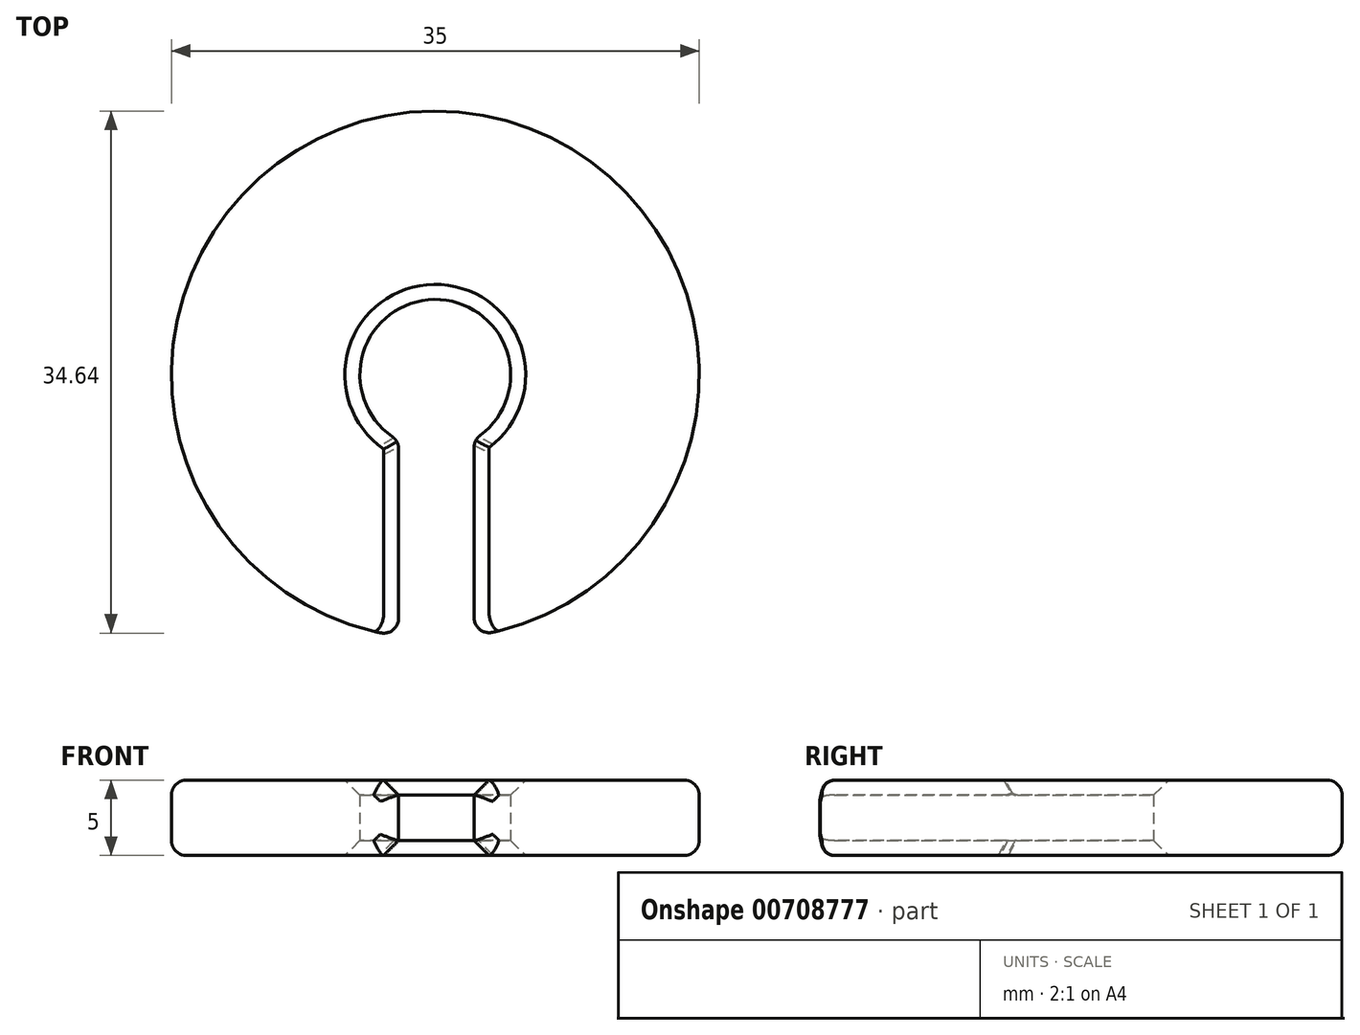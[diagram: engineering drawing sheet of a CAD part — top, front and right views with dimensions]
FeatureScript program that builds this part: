
annotation { "Feature Type Name" : "Feature", "Feature Type Description" : "" }
export const myFeature = defineFeature(function(context is Context, id is Id, definition is map)
    precondition{}
    {
        {
            var Q0;
            Q0=qCreatedBy(makeId("Top.planeOp"),FACE);
            var sketch = newSketch(context, id + "F0", { "sketchPlane" : qUnion([Q0])});
            skCircle(sketch, "E0", {"center": v(-4.66, 0) * mm, "radius": 5 * mm});
            skCircle(sketch, "E1", {"center": v(-4.66, 0) * mm, "radius": 17.5 * mm});
            skLineSegment(sketch, "E2", {"start": v(-7.08, -4.37) * mm, "end": v(-7.08, -24.29) * mm});
            skLineSegment(sketch, "E3", {"start": v(-7.08, -24.29) * mm, "end": v(-2.08, -24.29) * mm});
            skLineSegment(sketch, "E4", {"start": v(-2.08, -24.29) * mm, "end": v(-2.08, -4.29) * mm});
            skSolve(sketch);
        }
        {
            var Q0;
            {var subQ0=sQuery(id+"F0.wireOp",EDGE,"E2");var subQ1=sQuery(id+"F0.wireOp",EDGE,"E0");var subQ2=makeQuery(id+"F0.imprint","INTERSECT",VERTEX,{"derivedFrom":[subQ1,subQ0]});Q0=makeQuery(id+"F0.imprint","IMPRINT",FACE,{"disambiguationData":[TD([[makeQuery(id+"F0.imprint","IMPRINT",EDGE,{"disambiguationData":[TD([[subQ2,1.0]])],"derivedFrom":subQ1}),-1.0]])]});}
            extrude(context, id + "F1", {"entities" : qUnion([Q0]), "depth" : 5 * mm, "offsetDistance" : 25.4 * mm});
        }
        {
            var Q0;
            Q0=makeQuery(id+"F1.opExtrude","CAP_EDGE",EDGE,{"disambiguationData":[OSD([sQuery(id+"F0.wireOp",EDGE,"E2")])],"isStart":false});
            var Q1;
            Q1=makeQuery(id+"F1.opExtrude","CAP_EDGE",EDGE,{"disambiguationData":[OSD([sQuery(id+"F0.wireOp",EDGE,"E0")])],"isStart":false});
            var Q2;
            Q2=makeQuery(id+"F1.opExtrude","CAP_EDGE",EDGE,{"disambiguationData":[OSD([sQuery(id+"F0.wireOp",EDGE,"E4")])],"isStart":false});
            var Q3;
            Q3=makeQuery(id+"F1.opExtrude","CAP_EDGE",EDGE,{"disambiguationData":[OSD([sQuery(id+"F0.wireOp",EDGE,"E2")])],"isStart":true});
            var Q4;
            Q4=makeQuery(id+"F1.opExtrude","CAP_EDGE",EDGE,{"disambiguationData":[OSD([sQuery(id+"F0.wireOp",EDGE,"E4")])],"isStart":true});
            var Q5;
            Q5=makeQuery(id+"F1.opExtrude","CAP_EDGE",EDGE,{"disambiguationData":[OSD([sQuery(id+"F0.wireOp",EDGE,"E0")])],"isStart":true});
            chamfer(context, id + "F2", {"entities" : qUnion([Q0, Q1, Q2, Q3, Q4, Q5]), "width" : 1 * mm, "tangentPropagation" : true});
        }
        {
            var Q0;
            Q0=makeQuery(id+"F1.opExtrude","CAP_EDGE",EDGE,{"disambiguationData":[OSD([sQuery(id+"F0.wireOp",EDGE,"E1")])],"isStart":true});
            var Q1;
            Q1=makeQuery(id+"F1.opExtrude","CAP_EDGE",EDGE,{"disambiguationData":[OSD([sQuery(id+"F0.wireOp",EDGE,"E1")])],"isStart":false});
            var Q2;
            Q2=makeQuery(id+"F1.opExtrude","SWEPT_EDGE",EDGE,{"disambiguationData":[OSD([sQuery(id+"F0.wireOp",EDGE,"E1"),sQuery(id+"F0.wireOp",EDGE,"E4")])]});
            var Q3;
            Q3=makeQuery(id+"F2.opChamfer","BLEND_EDGE",EDGE,{"blendedFrom":[makeQuery(id+"F1.opExtrude","CAP_EDGE",EDGE,{"disambiguationData":[OSD([sQuery(id+"F0.wireOp",EDGE,"E4")])],"isStart":false}),makeQuery(id+"F1.opExtrude","SWEPT_FACE",FACE,{"disambiguationData":[OSD([sQuery(id+"F0.wireOp",EDGE,"E1")])]})],"blendedInto":[makeQuery(id+"F1.opExtrude","SWEPT_FACE",FACE,{"disambiguationData":[OSD([sQuery(id+"F0.wireOp",EDGE,"E1")])]})]});
            var Q4;
            Q4=makeQuery(id+"F2.opChamfer","BLEND_EDGE",EDGE,{"blendedFrom":[makeQuery(id+"F1.opExtrude","CAP_EDGE",EDGE,{"disambiguationData":[OSD([sQuery(id+"F0.wireOp",EDGE,"E4")])],"isStart":true}),makeQuery(id+"F1.opExtrude","SWEPT_FACE",FACE,{"disambiguationData":[OSD([sQuery(id+"F0.wireOp",EDGE,"E1")])]})],"blendedInto":[makeQuery(id+"F1.opExtrude","SWEPT_FACE",FACE,{"disambiguationData":[OSD([sQuery(id+"F0.wireOp",EDGE,"E1")])]})]});
            var Q5;
            Q5=makeQuery(id+"F2.opChamfer","BLEND_EDGE",EDGE,{"blendedFrom":[makeQuery(id+"F1.opExtrude","CAP_EDGE",EDGE,{"disambiguationData":[OSD([sQuery(id+"F0.wireOp",EDGE,"E2")])],"isStart":true}),makeQuery(id+"F1.opExtrude","SWEPT_FACE",FACE,{"disambiguationData":[OSD([sQuery(id+"F0.wireOp",EDGE,"E1")])]})],"blendedInto":[makeQuery(id+"F1.opExtrude","SWEPT_FACE",FACE,{"disambiguationData":[OSD([sQuery(id+"F0.wireOp",EDGE,"E1")])]})]});
            var Q6;
            Q6=makeQuery(id+"F1.opExtrude","SWEPT_EDGE",EDGE,{"disambiguationData":[OSD([sQuery(id+"F0.wireOp",EDGE,"E1"),sQuery(id+"F0.wireOp",EDGE,"E2")])]});
            var Q7;
            Q7=makeQuery(id+"F2.opChamfer","BLEND_EDGE",EDGE,{"blendedFrom":[makeQuery(id+"F1.opExtrude","CAP_EDGE",EDGE,{"disambiguationData":[OSD([sQuery(id+"F0.wireOp",EDGE,"E2")])],"isStart":false}),makeQuery(id+"F1.opExtrude","SWEPT_FACE",FACE,{"disambiguationData":[OSD([sQuery(id+"F0.wireOp",EDGE,"E1")])]})],"blendedInto":[makeQuery(id+"F1.opExtrude","SWEPT_FACE",FACE,{"disambiguationData":[OSD([sQuery(id+"F0.wireOp",EDGE,"E1")])]})]});
            var Q8;
            Q8=makeQuery(id+"F1.opExtrude","SWEPT_EDGE",EDGE,{"disambiguationData":[OSD([sQuery(id+"F0.wireOp",EDGE,"E0"),sQuery(id+"F0.wireOp",EDGE,"E4")])]});
            var Q9;
            Q9=makeQuery(id+"F2.opChamfer","BLEND_EDGE",EDGE,{"blendedFrom":[makeQuery(id+"F1.opExtrude","CAP_EDGE",EDGE,{"disambiguationData":[OSD([sQuery(id+"F0.wireOp",EDGE,"E0")])],"isStart":true}),makeQuery(id+"F1.opExtrude","CAP_EDGE",EDGE,{"disambiguationData":[OSD([sQuery(id+"F0.wireOp",EDGE,"E4")])],"isStart":true})],"blendedInto":[]});
            var Q10;
            Q10=makeQuery(id+"F2.opChamfer","BLEND_EDGE",EDGE,{"blendedFrom":[makeQuery(id+"F1.opExtrude","CAP_EDGE",EDGE,{"disambiguationData":[OSD([sQuery(id+"F0.wireOp",EDGE,"E0")])],"isStart":true}),makeQuery(id+"F1.opExtrude","CAP_EDGE",EDGE,{"disambiguationData":[OSD([sQuery(id+"F0.wireOp",EDGE,"E2")])],"isStart":true})],"blendedInto":[]});
            var Q11;
            Q11=makeQuery(id+"F1.opExtrude","SWEPT_EDGE",EDGE,{"disambiguationData":[OSD([sQuery(id+"F0.wireOp",EDGE,"E0"),sQuery(id+"F0.wireOp",EDGE,"E2")])]});
            fillet(context, id + "F3", {"entities" : qUnion([Q0, Q1, Q2, Q3, Q4, Q5, Q6, Q7, Q8, Q9, Q10, Q11]), "radius" : 1 * mm, "tangentPropagation" : true, "allowEdgeOverflow" : false});
        }
    });
